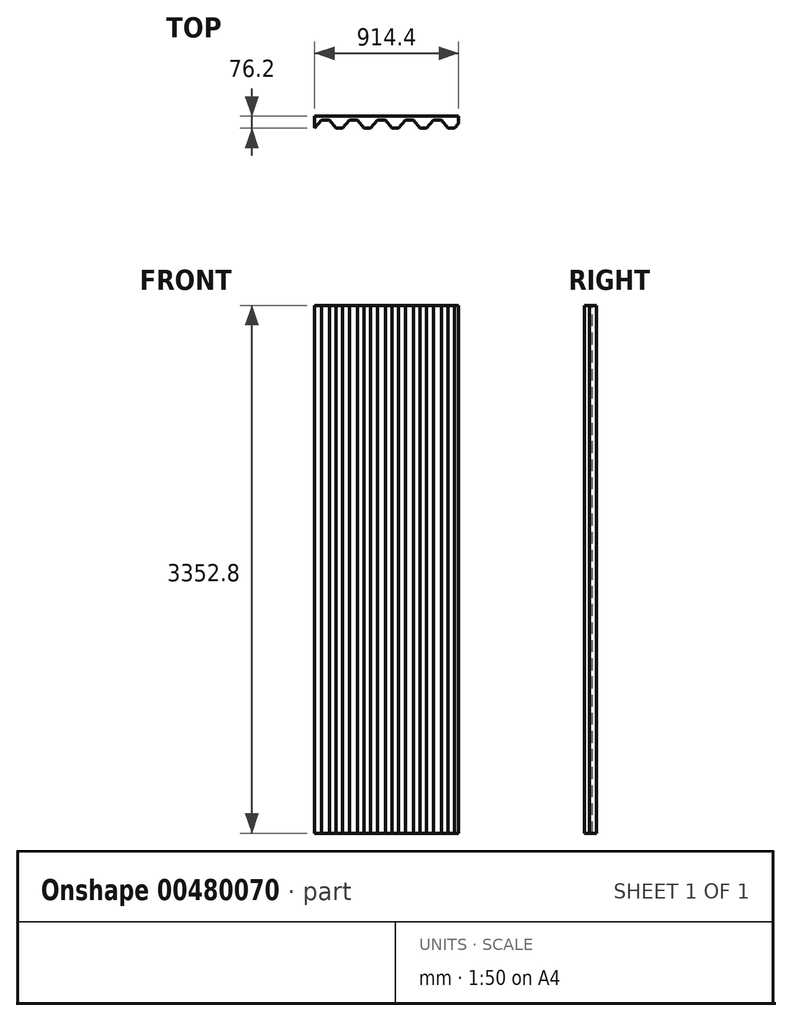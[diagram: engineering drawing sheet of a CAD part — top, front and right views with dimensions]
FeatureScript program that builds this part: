
annotation { "Feature Type Name" : "Feature", "Feature Type Description" : "" }
export const myFeature = defineFeature(function(context is Context, id is Id, definition is map)
    precondition{}
    {
        {
            var Q0;
            Q0=qCreatedBy(makeId("Top.planeOp"),FACE);
            var sketch = newSketch(context, id + "F0", { "sketchPlane" : qUnion([Q0])});
            skLineSegment(sketch, "E0.bottom", {"start": v(457.2, -50.8) * mm, "end": v(-457.2, -50.8) * mm});
            skLineSegment(sketch, "E0.top", {"start": v(457.2, 50.8) * mm, "end": v(-457.2, 50.8) * mm});
            skLineSegment(sketch, "E0.left", {"start": v(457.2, -50.8) * mm, "end": v(457.2, 50.8) * mm});
            skLineSegment(sketch, "E0.right", {"start": v(-457.2, -50.8) * mm, "end": v(-457.2, 50.8) * mm});
            skPoint(sketch, "E0.middle", {"position": v(0, 0) * mm});
            skSolve(sketch);
        }
        {
            var Q0;
            Q0 = qSketchRegion(id + "F0", true);
            extrude(context, id + "F1", {"entities" : qUnion([Q0]), "depth" : 3352.8 * mm});
        }
        {
            var Q0;
            Q0=makeQuery(id+"F1.opExtrude","CAP_FACE",FACE,{"disambiguationData":[OSD([sQuery(id+"F0.wireOp",EDGE,"E0.bottom"),sQuery(id+"F0.wireOp",EDGE,"E0.top"),sQuery(id+"F0.wireOp",EDGE,"E0.left"),sQuery(id+"F0.wireOp",EDGE,"E0.right")])],"isStart":false});
            var sketch = newSketch(context, id + "F2", { "sketchPlane" : qUnion([Q0])});
            skLineSegment(sketch, "E1", {"start": v(-457.2, 0) * mm, "end": v(-457.2, 25.4) * mm, "construction": true});
            skLineSegment(sketch, "E2", {"start": v(-457.2, 0) * mm, "end": v(-457.2, -25.4) * mm, "construction": true});
            skLineSegment(sketch, "E3", {"start": v(-457.2, -25.4) * mm, "end": v(-414.57, 25.4) * mm});
            skLineSegment(sketch, "E4", {"start": v(-414.57, 25.4) * mm, "end": v(-363.77, 25.4) * mm});
            skLineSegment(sketch, "E5", {"start": v(-363.77, 25.4) * mm, "end": v(-321.15, -25.4) * mm});
            skLineSegment(sketch, "E6", {"start": v(-321.15, -25.4) * mm, "end": v(-279.4, -25.4) * mm});
            skLineSegment(sketch, "E7.1.0.0", {"start": v(-279.4, -25.4) * mm, "end": v(-236.77, 25.4) * mm});
            skLineSegment(sketch, "E7.1.0.1", {"start": v(-236.77, 25.4) * mm, "end": v(-185.97, 25.4) * mm});
            skLineSegment(sketch, "E7.1.0.2", {"start": v(-185.97, 25.4) * mm, "end": v(-143.35, -25.4) * mm});
            skLineSegment(sketch, "E7.1.0.3", {"start": v(-143.35, -25.4) * mm, "end": v(-101.6, -25.4) * mm});
            skLineSegment(sketch, "E7.2.0.0", {"start": v(-101.6, -25.4) * mm, "end": v(-58.97, 25.4) * mm});
            skLineSegment(sketch, "E7.2.0.1", {"start": v(-58.97, 25.4) * mm, "end": v(-8.17, 25.4) * mm});
            skLineSegment(sketch, "E7.2.0.2", {"start": v(-8.17, 25.4) * mm, "end": v(34.45, -25.4) * mm});
            skLineSegment(sketch, "E7.2.0.3", {"start": v(34.45, -25.4) * mm, "end": v(76.2, -25.4) * mm});
            skLineSegment(sketch, "E7.3.0.0", {"start": v(76.2, -25.4) * mm, "end": v(118.83, 25.4) * mm});
            skLineSegment(sketch, "E7.3.0.1", {"start": v(118.83, 25.4) * mm, "end": v(169.63, 25.4) * mm});
            skLineSegment(sketch, "E7.3.0.2", {"start": v(169.63, 25.4) * mm, "end": v(212.25, -25.4) * mm});
            skLineSegment(sketch, "E7.3.0.3", {"start": v(212.25, -25.4) * mm, "end": v(254, -25.4) * mm});
            skLineSegment(sketch, "E7.4.0.0", {"start": v(254, -25.4) * mm, "end": v(296.63, 25.4) * mm});
            skLineSegment(sketch, "E7.4.0.1", {"start": v(296.63, 25.4) * mm, "end": v(347.43, 25.4) * mm});
            skLineSegment(sketch, "E7.4.0.2", {"start": v(347.43, 25.4) * mm, "end": v(390.05, -25.4) * mm});
            skLineSegment(sketch, "E7.4.0.3", {"start": v(390.05, -25.4) * mm, "end": v(431.8, -25.4) * mm});
            skLineSegment(sketch, "E7.5.0.0", {"start": v(431.8, -25.4) * mm, "end": v(457.2, 4.87) * mm});
            skLineSegment(sketch, "E7.direction1", {"start": v(-457.2, -25.4) * mm, "end": v(-279.4, -25.4) * mm, "construction": true});
            skPoint(sketch, "E8", {"position": v(457.2, 4.87) * mm});
            skPoint(sketch, "E9.orphan", {"position": v(474.43, 25.4) * mm});
            skSolve(sketch);
        }
        {
            var Q0;
            Q0 = qSketchRegion(id + "F2", true);
            var Q1;
            {var subQ2=sQuery(id+"F2.wireOp",EDGE,"E3");Q1=makeQuery(id+"F2.imprint","IMPRINT",FACE,{"disambiguationData":[TD([[makeQuery(id+"F2.imprint","IMPRINT",EDGE,{"derivedFrom":subQ2}),-1.0]])]});}
            extrude(context, id + "F3", {"entities" : qUnion([Q0, Q1]), "operationType" : NewBodyOperationType.REMOVE, "endBound" : BoundingType.THROUGH_ALL, "oppositeDirection" : true, "depth" : 25.4 * mm});
        }
    });
